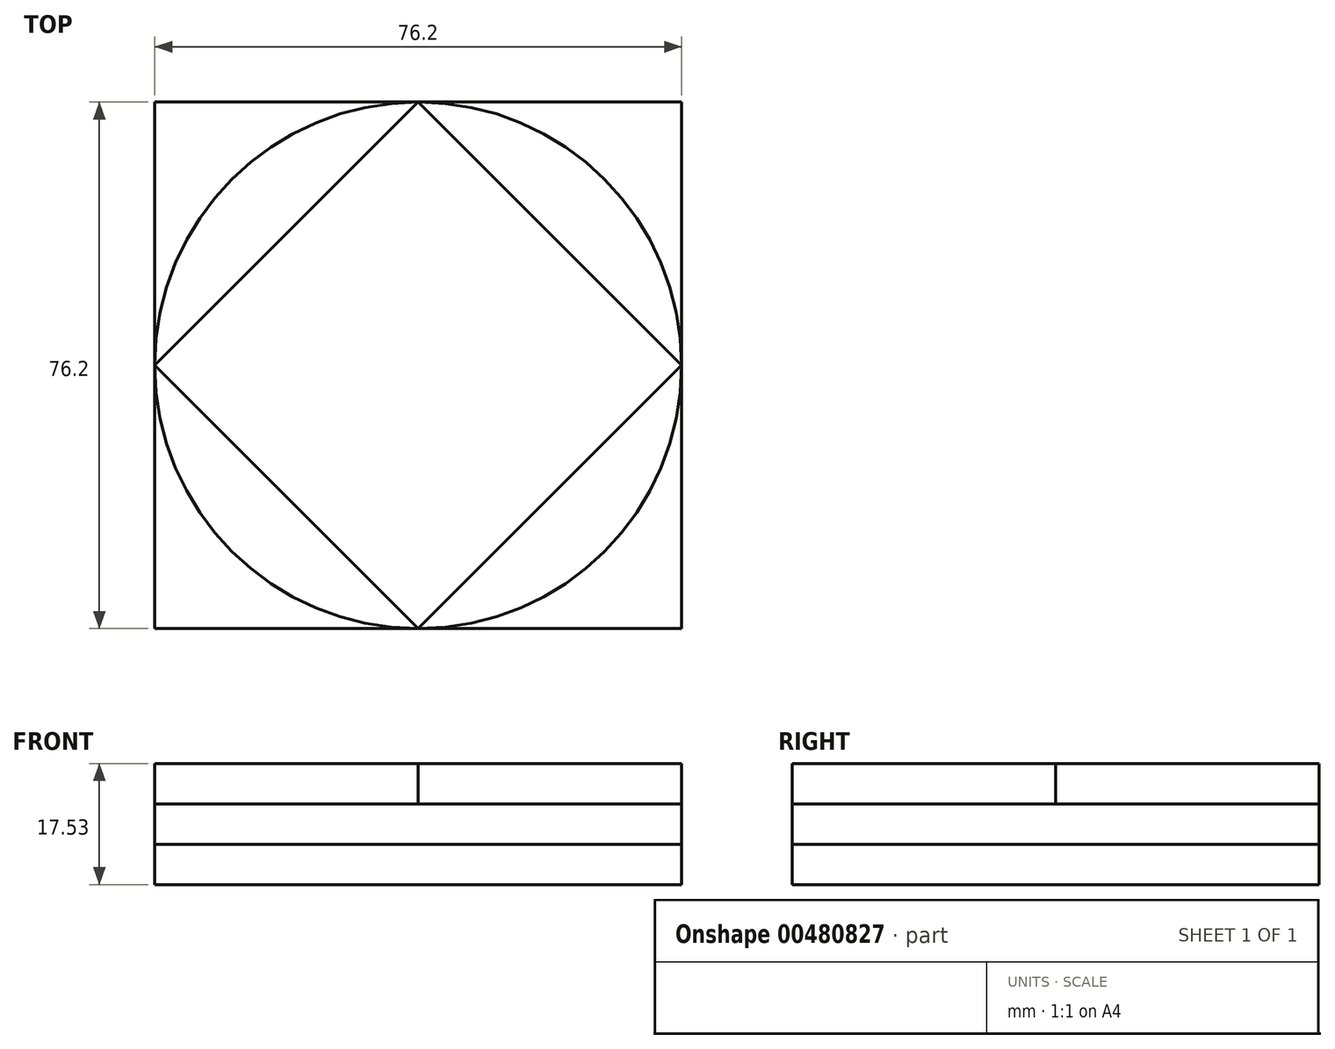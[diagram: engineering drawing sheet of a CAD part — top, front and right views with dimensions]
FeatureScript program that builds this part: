
annotation { "Feature Type Name" : "Feature", "Feature Type Description" : "" }
export const myFeature = defineFeature(function(context is Context, id is Id, definition is map)
    precondition{}
    {
        {
            var Q0;
            Q0=qCreatedBy(makeId("Top.planeOp"),FACE);
            var sketch = newSketch(context, id + "F0", { "sketchPlane" : qUnion([Q0])});
            skLineSegment(sketch, "E0.bottom", {"start": v(-6.01, -3.8) * mm, "end": v(70.19, -3.8) * mm});
            skLineSegment(sketch, "E0.top", {"start": v(-6.01, 72.4) * mm, "end": v(70.19, 72.4) * mm});
            skLineSegment(sketch, "E0.left", {"start": v(-6.01, -3.8) * mm, "end": v(-6.01, 72.4) * mm});
            skLineSegment(sketch, "E0.right", {"start": v(70.19, -3.8) * mm, "end": v(70.19, 72.4) * mm});
            skSolve(sketch);
        }
        {
            var Q0;
            Q0=makeQuery(id+"F0.imprint","IMPRINT",FACE,{"disambiguationData":[TD([[makeQuery(id+"F0.imprint","IMPRINT",EDGE,{"derivedFrom":sQuery(id+"F0.wireOp",EDGE,"E0.bottom")}),1.0]])]});
            extrude(context, id + "F1", {"entities" : qUnion([Q0]), "depth" : 5.84 * mm});
        }
        {
            var Q0;
            Q0=makeQuery(id+"F1.opExtrude","CAP_FACE",FACE,{"disambiguationData":[OSD([sQuery(id+"F0.wireOp",EDGE,"E0.bottom"),sQuery(id+"F0.wireOp",EDGE,"E0.top"),sQuery(id+"F0.wireOp",EDGE,"E0.left"),sQuery(id+"F0.wireOp",EDGE,"E0.right")])],"isStart":false});
            var sketch = newSketch(context, id + "F2", { "sketchPlane" : qUnion([Q0])});
            skCircle(sketch, "E1", {"center": v(32.09, 34.3) * mm, "radius": 38.1 * mm});
            skSolve(sketch);
        }
        {
            var Q0;
            Q0 = qSketchRegion(id + "F2", true);
            extrude(context, id + "F3", {"entities" : qUnion([Q0]), "operationType" : NewBodyOperationType.ADD, "depth" : 5.84 * mm});
        }
        {
            var Q0;
            Q0=makeQuery(id+"F3.opExtrude","CAP_FACE",FACE,{"disambiguationData":[OSD([sQuery(id+"F2.wireOp",EDGE,"E1")])],"isStart":false});
            var sketch = newSketch(context, id + "F4", { "sketchPlane" : qUnion([Q0])});
            skLineSegment(sketch, "E2", {"start": v(32.09, 72.4) * mm, "end": v(70.19, 34.3) * mm});
            skLineSegment(sketch, "E3", {"start": v(70.19, 34.3) * mm, "end": v(32.09, -3.8) * mm});
            skLineSegment(sketch, "E4", {"start": v(32.09, -3.8) * mm, "end": v(-6.01, 34.3) * mm});
            skLineSegment(sketch, "E5", {"start": v(-6.01, 34.3) * mm, "end": v(32.09, 72.4) * mm});
            skSolve(sketch);
        }
        {
            var Q0;
            Q0 = qSketchRegion(id + "F4", true);
            extrude(context, id + "F5", {"entities" : qUnion([Q0]), "operationType" : NewBodyOperationType.ADD, "depth" : 5.84 * mm});
        }
    });
